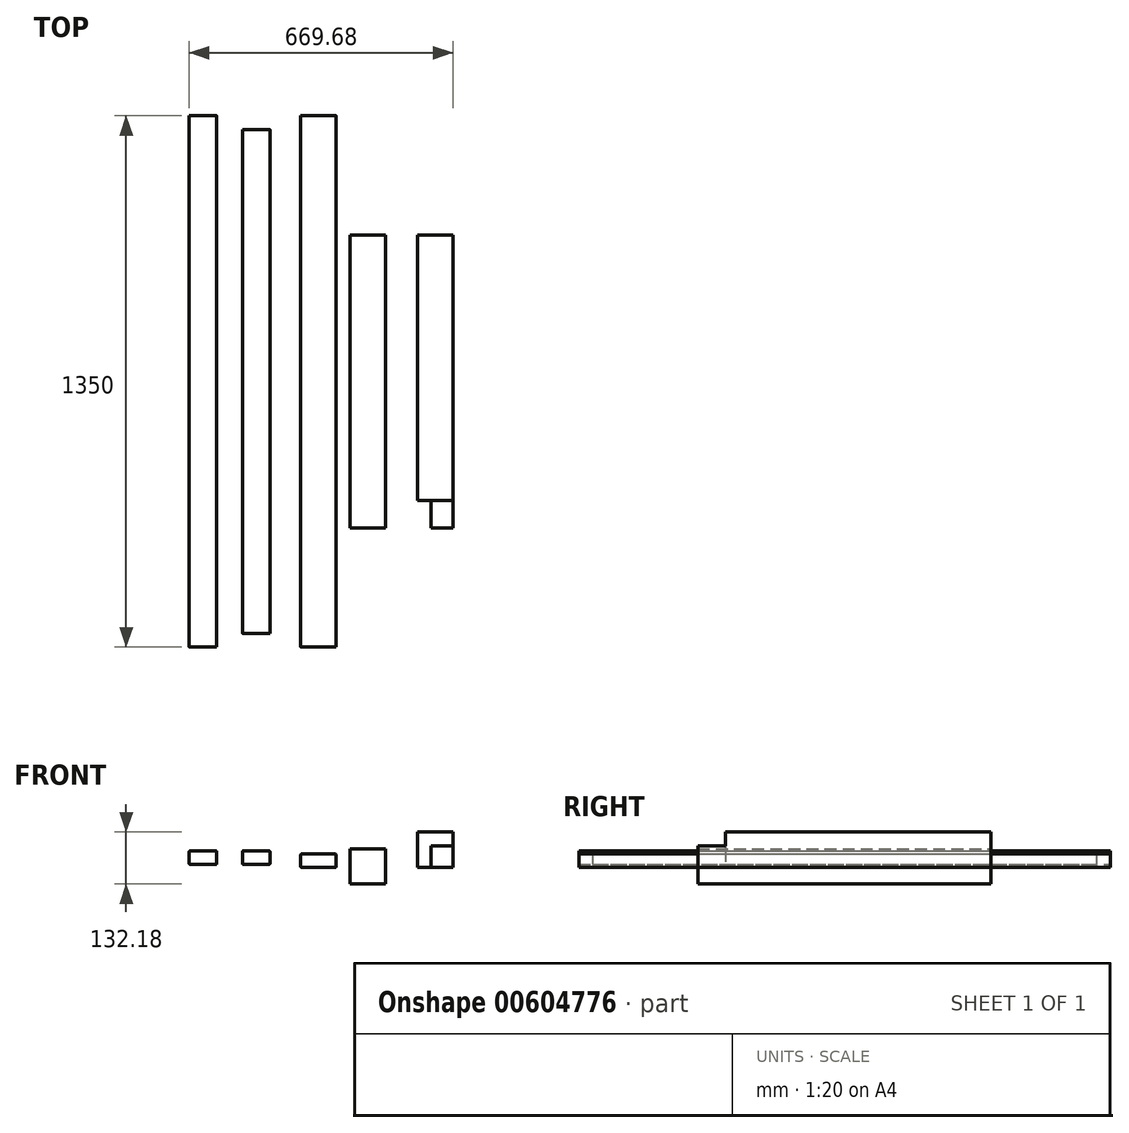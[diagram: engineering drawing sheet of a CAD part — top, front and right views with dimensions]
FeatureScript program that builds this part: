
annotation { "Feature Type Name" : "Feature", "Feature Type Description" : "" }
export const myFeature = defineFeature(function(context is Context, id is Id, definition is map)
    precondition{}
    {
        {
            var Q0;
            Q0=qCreatedBy(makeId("Front.planeOp"),FACE);
            var sketch = newSketch(context, id + "F0", { "sketchPlane" : qUnion([Q0])});
            skLineSegment(sketch, "E0.bottom", {"start": v(-44.52, 17.64) * mm, "end": v(45.48, 17.64) * mm});
            skLineSegment(sketch, "E0.top", {"start": v(-44.52, -17.36) * mm, "end": v(45.48, -17.36) * mm});
            skLineSegment(sketch, "E0.left", {"start": v(-44.52, 17.64) * mm, "end": v(-44.52, -17.36) * mm});
            skLineSegment(sketch, "E0.right", {"start": v(45.48, 17.64) * mm, "end": v(45.48, -17.36) * mm});
            skSolve(sketch);
        }
        {
            var Q0;
            Q0=makeQuery(id+"F0.imprint","IMPRINT",FACE,{"disambiguationData":[TD([[makeQuery(id+"F0.imprint","IMPRINT",EDGE,{"derivedFrom":sQuery(id+"F0.wireOp",EDGE,"E0.bottom")}),-1.0]])]});
            extrude(context, id + "F1", {"entities" : qUnion([Q0]), "endBound" : BoundingType.SYMMETRIC, "depth" : 1350 * mm, "offsetDistance" : 25 * mm});
        }
        {
            var Q0;
            Q0=makeQuery(id+"F1.opExtrude","SWEPT_EDGE",EDGE,{"disambiguationData":[OSD([sQuery(id+"F0.wireOp",EDGE,"E0.bottom"),sQuery(id+"F0.wireOp",EDGE,"E0.right")])]});
            var Q1;
            Q1=makeQuery(id+"F1.opExtrude","SWEPT_EDGE",EDGE,{"disambiguationData":[OSD([sQuery(id+"F0.wireOp",EDGE,"E0.top"),sQuery(id+"F0.wireOp",EDGE,"E0.right")])]});
            var Q2;
            Q2=makeQuery(id+"F1.opExtrude","SWEPT_EDGE",EDGE,{"disambiguationData":[OSD([sQuery(id+"F0.wireOp",EDGE,"E0.bottom"),sQuery(id+"F0.wireOp",EDGE,"E0.left")])]});
            var Q3;
            Q3=makeQuery(id+"F1.opExtrude","SWEPT_EDGE",EDGE,{"disambiguationData":[OSD([sQuery(id+"F0.wireOp",EDGE,"E0.top"),sQuery(id+"F0.wireOp",EDGE,"E0.left")])]});
            fillet(context, id + "F2", {"entities" : qUnion([Q0, Q1, Q2, Q3]), "radius" : 3 * mm, "tangentPropagation" : true, "allowEdgeOverflow" : false});
        }
        {
            var Q0;
            Q0=qCreatedBy(makeId("Front.planeOp"),FACE);
            var sketch = newSketch(context, id + "F3", { "sketchPlane" : qUnion([Q0])});
            skLineSegment(sketch, "E1.bottom", {"start": v(80.92, 30.7) * mm, "end": v(170.92, 30.7) * mm});
            skLineSegment(sketch, "E1.top", {"start": v(80.92, -59.3) * mm, "end": v(170.92, -59.3) * mm});
            skLineSegment(sketch, "E1.left", {"start": v(80.92, 30.7) * mm, "end": v(80.92, -59.3) * mm});
            skLineSegment(sketch, "E1.right", {"start": v(170.92, 30.7) * mm, "end": v(170.92, -59.3) * mm});
            skSolve(sketch);
        }
        {
            var Q0;
            Q0=makeQuery(id+"F3.imprint","IMPRINT",FACE,{"disambiguationData":[TD([[makeQuery(id+"F3.imprint","IMPRINT",EDGE,{"derivedFrom":sQuery(id+"F3.wireOp",EDGE,"E1.bottom")}),-1.0]])]});
            extrude(context, id + "F4", {"entities" : qUnion([Q0]), "endBound" : BoundingType.SYMMETRIC, "depth" : (780 - 35) * mm, "offsetDistance" : 25 * mm});
        }
        {
            var Q0;
            Q0=qCreatedBy(makeId("Front.planeOp"),FACE);
            var sketch = newSketch(context, id + "F5", { "sketchPlane" : qUnion([Q0])});
            skLineSegment(sketch, "E2.bottom", {"start": v(-192.86, 25.59) * mm, "end": v(-122.86, 25.59) * mm});
            skLineSegment(sketch, "E2.top", {"start": v(-192.86, -9.41) * mm, "end": v(-122.86, -9.41) * mm});
            skLineSegment(sketch, "E2.left", {"start": v(-192.86, 25.59) * mm, "end": v(-192.86, -9.41) * mm});
            skLineSegment(sketch, "E2.right", {"start": v(-122.86, 25.59) * mm, "end": v(-122.86, -9.41) * mm});
            skSolve(sketch);
        }
        {
            var Q0;
            Q0=makeQuery(id+"F5.imprint","IMPRINT",FACE,{"disambiguationData":[TD([[makeQuery(id+"F5.imprint","IMPRINT",EDGE,{"derivedFrom":sQuery(id+"F5.wireOp",EDGE,"E2.bottom")}),-1.0]])]});
            extrude(context, id + "F6", {"entities" : qUnion([Q0]), "endBound" : BoundingType.SYMMETRIC, "depth" : (1350 - 70) * mm, "offsetDistance" : 25 * mm});
        }
        {
            var Q0;
            Q0=makeQuery(id+"F6.opExtrude","SWEPT_EDGE",EDGE,{"disambiguationData":[OSD([sQuery(id+"F5.wireOp",EDGE,"E2.bottom"),sQuery(id+"F5.wireOp",EDGE,"E2.right")])]});
            var Q1;
            Q1=makeQuery(id+"F6.opExtrude","SWEPT_EDGE",EDGE,{"disambiguationData":[OSD([sQuery(id+"F5.wireOp",EDGE,"E2.top"),sQuery(id+"F5.wireOp",EDGE,"E2.right")])]});
            var Q2;
            Q2=makeQuery(id+"F6.opExtrude","SWEPT_EDGE",EDGE,{"disambiguationData":[OSD([sQuery(id+"F5.wireOp",EDGE,"E2.bottom"),sQuery(id+"F5.wireOp",EDGE,"E2.left")])]});
            var Q3;
            Q3=makeQuery(id+"F6.opExtrude","SWEPT_EDGE",EDGE,{"disambiguationData":[OSD([sQuery(id+"F5.wireOp",EDGE,"E2.top"),sQuery(id+"F5.wireOp",EDGE,"E2.left")])]});
            fillet(context, id + "F7", {"entities" : qUnion([Q0, Q1, Q2, Q3]), "radius" : 3 * mm, "tangentPropagation" : true, "allowEdgeOverflow" : false});
        }
        {
            var Q0;
            Q0=qCreatedBy(makeId("Front.planeOp"),FACE);
            var sketch = newSketch(context, id + "F8", { "sketchPlane" : qUnion([Q0])});
            skLineSegment(sketch, "E3.bottom", {"start": v(-327.87, 25.6) * mm, "end": v(-257.87, 25.6) * mm});
            skLineSegment(sketch, "E3.top", {"start": v(-327.87, -9.4) * mm, "end": v(-257.87, -9.4) * mm});
            skLineSegment(sketch, "E3.left", {"start": v(-327.87, 25.6) * mm, "end": v(-327.87, -9.4) * mm});
            skLineSegment(sketch, "E3.right", {"start": v(-257.87, 25.6) * mm, "end": v(-257.87, -9.4) * mm});
            skSolve(sketch);
        }
        {
            var Q0;
            Q0=makeQuery(id+"F8.imprint","IMPRINT",FACE,{"disambiguationData":[TD([[makeQuery(id+"F8.imprint","IMPRINT",EDGE,{"derivedFrom":sQuery(id+"F8.wireOp",EDGE,"E3.bottom")}),-1.0]])]});
            extrude(context, id + "F9", {"entities" : qUnion([Q0]), "endBound" : BoundingType.SYMMETRIC, "depth" : 1350 * mm, "offsetDistance" : 25 * mm});
        }
        {
            var Q0;
            Q0=makeQuery(id+"F9.opExtrude","SWEPT_EDGE",EDGE,{"disambiguationData":[OSD([sQuery(id+"F8.wireOp",EDGE,"E3.top"),sQuery(id+"F8.wireOp",EDGE,"E3.left")])]});
            var Q1;
            Q1=makeQuery(id+"F9.opExtrude","SWEPT_EDGE",EDGE,{"disambiguationData":[OSD([sQuery(id+"F8.wireOp",EDGE,"E3.bottom"),sQuery(id+"F8.wireOp",EDGE,"E3.left")])]});
            var Q2;
            Q2=makeQuery(id+"F9.opExtrude","SWEPT_EDGE",EDGE,{"disambiguationData":[OSD([sQuery(id+"F8.wireOp",EDGE,"E3.bottom"),sQuery(id+"F8.wireOp",EDGE,"E3.right")])]});
            var Q3;
            Q3=makeQuery(id+"F9.opExtrude","SWEPT_EDGE",EDGE,{"disambiguationData":[OSD([sQuery(id+"F8.wireOp",EDGE,"E3.top"),sQuery(id+"F8.wireOp",EDGE,"E3.right")])]});
            fillet(context, id + "F10", {"entities" : qUnion([Q0, Q1, Q2, Q3]), "radius" : 3 * mm, "tangentPropagation" : true, "allowEdgeOverflow" : false});
        }
        {
            var Q0;
            Q0=qCreatedBy(makeId("Front.planeOp"),FACE);
            var sketch = newSketch(context, id + "F11", { "sketchPlane" : qUnion([Q0])});
            skLineSegment(sketch, "E4.bottom", {"start": v(251.8, 72.88) * mm, "end": v(341.8, 72.88) * mm});
            skLineSegment(sketch, "E4.top", {"start": v(251.8, -17.12) * mm, "end": v(341.8, -17.12) * mm});
            skLineSegment(sketch, "E4.left", {"start": v(251.8, 72.88) * mm, "end": v(251.8, -17.12) * mm});
            skLineSegment(sketch, "E4.right", {"start": v(341.8, 72.88) * mm, "end": v(341.8, -17.12) * mm});
            skSolve(sketch);
        }
        {
            var Q0;
            Q0=makeQuery(id+"F11.imprint","IMPRINT",FACE,{"disambiguationData":[TD([[makeQuery(id+"F11.imprint","IMPRINT",EDGE,{"derivedFrom":sQuery(id+"F11.wireOp",EDGE,"E4.bottom")}),-1.0]])]});
            extrude(context, id + "F12", {"entities" : qUnion([Q0]), "endBound" : BoundingType.SYMMETRIC, "depth" : (780 - 35) * mm, "offsetDistance" : 25 * mm});
        }
        {
            var Q0;
            Q0=makeQuery(id+"F12.opExtrude","CAP_FACE",FACE,{"disambiguationData":[OSD([sQuery(id+"F11.wireOp",EDGE,"E4.bottom"),sQuery(id+"F11.wireOp",EDGE,"E4.top"),sQuery(id+"F11.wireOp",EDGE,"E4.left"),sQuery(id+"F11.wireOp",EDGE,"E4.right")])],"isStart":false});
            var sketch = newSketch(context, id + "F13", { "sketchPlane" : qUnion([Q0])});
            skLineSegment(sketch, "E5.bottom", {"start": v(251.8, 72.88) * mm, "end": v(286.8, 72.88) * mm});
            skLineSegment(sketch, "E5.top", {"start": v(251.8, -17.12) * mm, "end": v(286.8, -17.12) * mm});
            skLineSegment(sketch, "E5.left", {"start": v(251.8, 72.88) * mm, "end": v(251.8, -17.12) * mm});
            skLineSegment(sketch, "E5.right", {"start": v(286.8, 72.88) * mm, "end": v(286.8, -17.12) * mm});
            skLineSegment(sketch, "E6.bottom", {"start": v(251.8, 72.88) * mm, "end": v(341.8, 72.88) * mm});
            skLineSegment(sketch, "E6.top", {"start": v(251.8, 37.88) * mm, "end": v(341.8, 37.88) * mm});
            skLineSegment(sketch, "E6.left", {"start": v(251.8, 72.88) * mm, "end": v(251.8, 37.88) * mm});
            skLineSegment(sketch, "E6.right", {"start": v(341.8, 72.88) * mm, "end": v(341.8, 37.88) * mm});
            skSolve(sketch);
        }
        {
            var Q0;
            Q0 = qSketchRegion(id + "F13", true);
            extrude(context, id + "F14", {"entities" : qUnion([Q0]), "operationType" : NewBodyOperationType.REMOVE, "oppositeDirection" : true, "depth" : 70 * mm, "offsetDistance" : 25 * mm});
        }
    });
